# Revit family: Urinal-Wash_Down-Sloan-Top_Spud-(SU-7006_SU-7009)_Series
name_source: partatom
category: Plumbing Fixtures
revit_build: Autodesk Revit 2014 (Build: 20130308_1515(x64)
units: mm (PartAtom-declared; Revit-internal decimal feet)

## types (4) — shared parameters
ADA Compliant = Yes
Assembly Code = D2010210
CW Connection = Yes
CWFU = 5
Cold Water Connection Diameter = 3/4"
Cold Water Connection Height = 11 1/2"
Cold Water Connection Radius = 3/8"
Cold Water Connection Width = 4 3/4"
Default Elevation = 17"
Flush Method = Washdown
Flush and Flow Rates = 1.0 gpf (3.8 Lpf)
HW Connection = No
Height = 23 1/2"
High-Efficiency = Yes
IAPMO Compliance = cUPC
Length = 14 3/4"
Manufacturer = Sloan
Material = Vitreous China-Sloan-White
Mounting = Wall Hung
Product Documentation Link = https://specifications.sloan.com
Product Page URL = https://www.sloan.com
Revised Date = 9/1/2015
Spud Location = Rear Spud
URL = http://www.sloan.com
Vent Connection = No
WFU = 5
Waste Connection = Yes
Waste Connection Diameter = 2"
Waste Connection Height = 18 3/8"
Waste Connection Radius = 1"
Width = 14 3/16"

## per-type parameters (varying)
| type | Description | Order Code |
| SU-7006 | Complete Vitreous China top spud small urinal. | 1107006 |
| SU-7006-STG | Small LC TS  Urinal w/ SloanTec Glaze | 1177006 |
| SU-7009 | Complete Vitreous China top spud small urinal. | 1107009 |
| SU-7009-STG | Complete Vitreous China top spud small urinal. | 1177009 |

note: column(s) folded — value = type name in every type: Model
